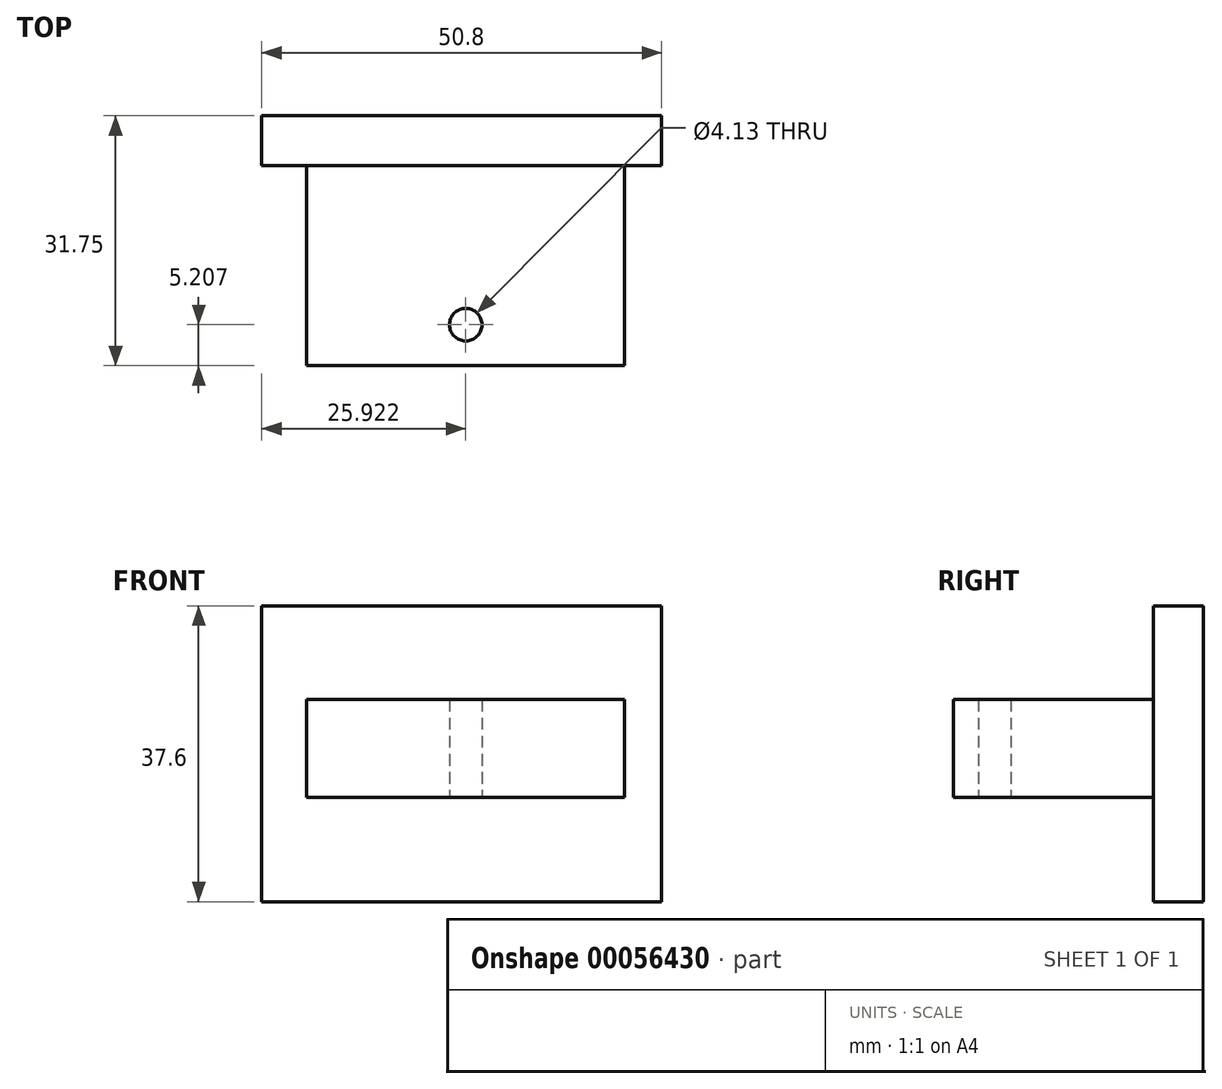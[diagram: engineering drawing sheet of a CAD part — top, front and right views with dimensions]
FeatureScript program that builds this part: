
annotation { "Feature Type Name" : "Feature", "Feature Type Description" : "" }
export const myFeature = defineFeature(function(context is Context, id is Id, definition is map)
    precondition{}
    {
        {
            var Q0;
            Q0=qCreatedBy(makeId("Front.planeOp"),FACE);
            var sketch = newSketch(context, id + "F0", { "sketchPlane" : qUnion([Q0])});
            skLineSegment(sketch, "E0.bottom", {"start": v(-69.65, 43.16) * mm, "end": v(-18.85, 43.16) * mm});
            skLineSegment(sketch, "E0.top", {"start": v(-69.65, 5.56) * mm, "end": v(-18.85, 5.56) * mm});
            skLineSegment(sketch, "E0.left", {"start": v(-69.65, 43.16) * mm, "end": v(-69.65, 5.56) * mm});
            skLineSegment(sketch, "E0.right", {"start": v(-18.85, 43.16) * mm, "end": v(-18.85, 5.56) * mm});
            skLineSegment(sketch, "E1.bottom", {"start": v(-63.92, 31.24) * mm, "end": v(-23.54, 31.24) * mm});
            skLineSegment(sketch, "E1.top", {"start": v(-63.92, 18.8) * mm, "end": v(-23.54, 18.8) * mm});
            skLineSegment(sketch, "E1.left", {"start": v(-63.92, 31.24) * mm, "end": v(-63.92, 18.8) * mm});
            skLineSegment(sketch, "E1.right", {"start": v(-23.54, 31.24) * mm, "end": v(-23.54, 18.8) * mm});
            skSolve(sketch);
        }
        {
            var Q0;
            Q0=makeQuery(id+"F0.imprint","IMPRINT",FACE,{"disambiguationData":[TD([[makeQuery(id+"F0.imprint","IMPRINT",EDGE,{"derivedFrom":sQuery(id+"F0.wireOp",EDGE,"E1.bottom")}),-1.0]])]});
            extrude(context, id + "F1", {"entities" : qUnion([Q0]), "depth" : 31.75 * mm});
        }
        {
            var Q0;
            Q0=makeQuery(id+"F0.imprint","IMPRINT",FACE,{"disambiguationData":[TD([[makeQuery(id+"F0.imprint","IMPRINT",EDGE,{"derivedFrom":sQuery(id+"F0.wireOp",EDGE,"E0.bottom")}),-1.0]])]});
            extrude(context, id + "F2", {"entities" : qUnion([Q0]), "operationType" : NewBodyOperationType.ADD, "depth" : 6.35 * mm});
        }
        {
            var Q0;
            Q0=makeQuery(id+"F1.opExtrude","SWEPT_FACE",FACE,{"disambiguationData":[OSD([sQuery(id+"F0.wireOp",EDGE,"E1.top")])]});
            var sketch = newSketch(context, id + "F3", { "sketchPlane" : qUnion([Q0])});
            skCircle(sketch, "E2", {"center": v(-43.73, 26.54) * mm, "radius": 20.2 * mm});
            skCircle(sketch, "E3", {"center": v(-43.73, 26.54) * mm, "radius": 2.06 * mm});
            skSolve(sketch);
        }
        {
            var Q0;
            Q0=makeQuery(id+"F3.imprint","IMPRINT",FACE,{"disambiguationData":[TD([[makeQuery(id+"F3.imprint","IMPRINT",EDGE,{"derivedFrom":sQuery(id+"F3.wireOp",EDGE,"E3")}),1.0]])]});
            extrude(context, id + "F4", {"entities" : qUnion([Q0]), "operationType" : NewBodyOperationType.REMOVE, "oppositeDirection" : true, "depth" : 62.67 * mm});
        }
    });
